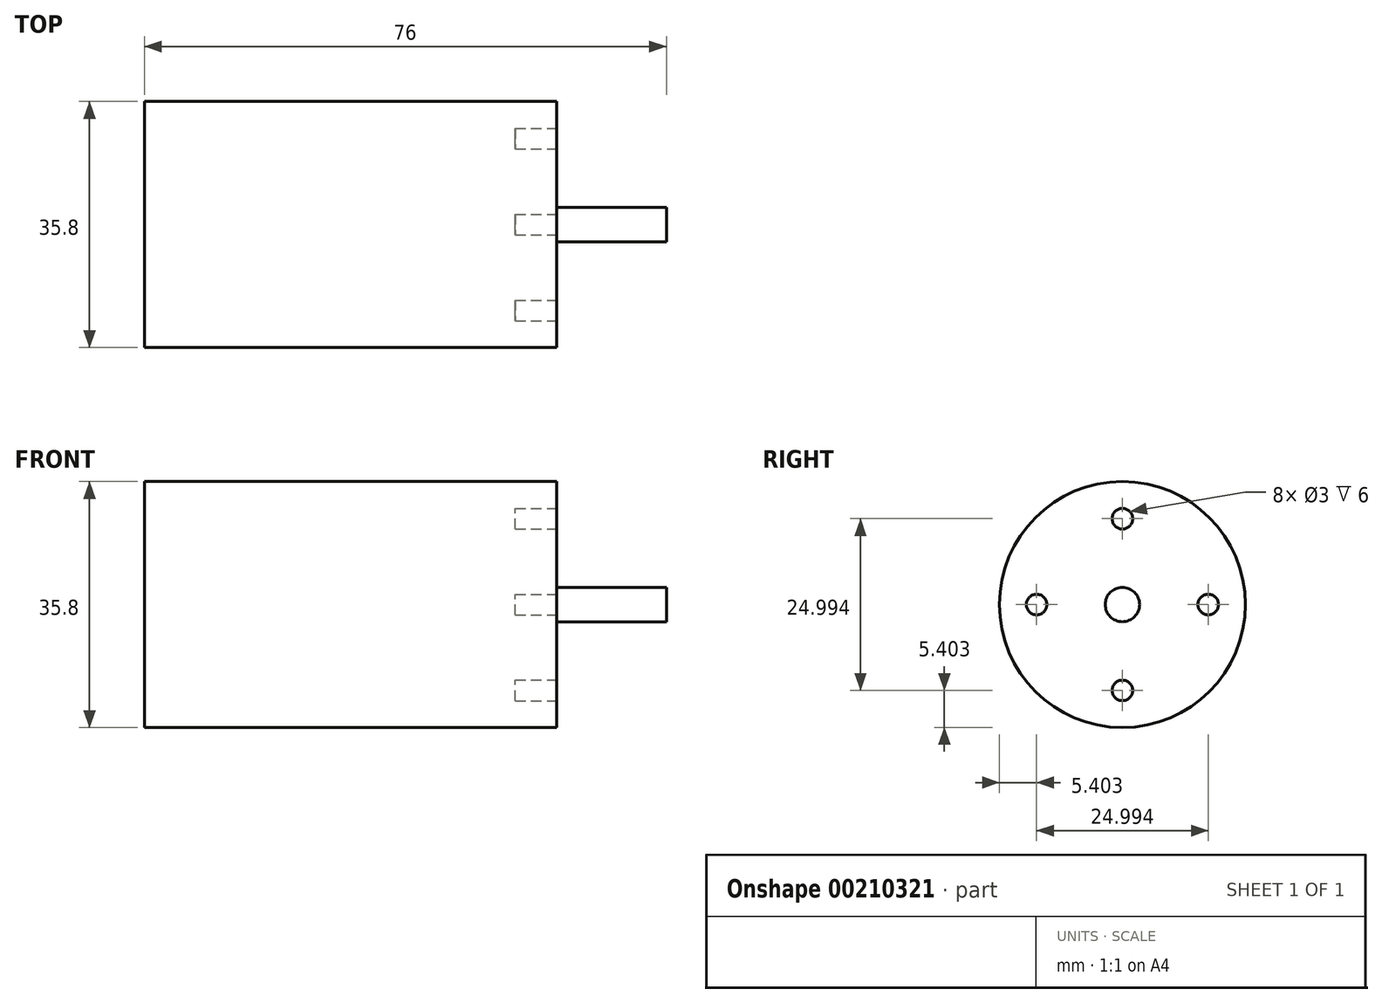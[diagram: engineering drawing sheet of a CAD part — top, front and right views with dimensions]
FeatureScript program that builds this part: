
annotation { "Feature Type Name" : "Feature", "Feature Type Description" : "" }
export const myFeature = defineFeature(function(context is Context, id is Id, definition is map)
    precondition{}
    {
        {
            var Q0;
            Q0=qCreatedBy(makeId("Right.planeOp"),FACE);
            var sketch = newSketch(context, id + "F0", { "sketchPlane" : qUnion([Q0])});
            skCircle(sketch, "E0", {"center": v(0, 0) * mm, "radius": 17.9 * mm});
            skSolve(sketch);
        }
        {
            var Q0;
            Q0 = qSketchRegion(id + "F0", true);
            extrude(context, id + "F1", {"entities" : qUnion([Q0]), "endBound" : BoundingType.SYMMETRIC, "depth" : 60 * mm});
        }
        {
            var Q0;
            Q0=makeQuery(id+"F1.opExtrude","CAP_FACE",FACE,{"disambiguationData":[OSD([sQuery(id+"F0.wireOp",EDGE,"E0")])],"isStart":false});
            var sketch = newSketch(context, id + "F2", { "sketchPlane" : qUnion([Q0])});
            skCircle(sketch, "E1", {"center": v(0, 0) * mm, "radius": 2.5 * mm});
            skSolve(sketch);
        }
        {
            var Q0;
            Q0 = qSketchRegion(id + "F2", true);
            extrude(context, id + "F3", {"entities" : qUnion([Q0]), "operationType" : NewBodyOperationType.ADD, "depth" : 16 * mm});
        }
        {
            var Q0;
            Q0=makeQuery(id+"F1.opExtrude","CAP_FACE",FACE,{"disambiguationData":[OSD([sQuery(id+"F0.wireOp",EDGE,"E0")])],"isStart":false});
            var sketch = newSketch(context, id + "F4", { "sketchPlane" : qUnion([Q0])});
            skCircle(sketch, "E2", {"center": v(0, 0) * mm, "radius": 12.5 * mm, "construction": true});
            skCircle(sketch, "E3", {"center": v(0, 12.5) * mm, "radius": 1.5 * mm});
            skCircle(sketch, "E4.1.0", {"center": v(-12.5, 0) * mm, "radius": 1.5 * mm});
            skCircle(sketch, "E4.2.0", {"center": v(0, -12.5) * mm, "radius": 1.5 * mm});
            skCircle(sketch, "E4.3.0", {"center": v(12.5, 0) * mm, "radius": 1.5 * mm});
            skSolve(sketch);
        }
        {
            var Q0;
            Q0 = qSketchRegion(id + "F4", true);
            extrude(context, id + "F5", {"entities" : qUnion([Q0]), "operationType" : NewBodyOperationType.REMOVE, "oppositeDirection" : true, "depth" : 6 * mm});
        }
        {
            var Q0;
            Q0=makeQuery(id+"F1.opExtrude","SWEPT_BODY",BODY,{"disambiguationData":[OSD([sQuery(id+"F0.wireOp",EDGE,"E0")])]});
            transform(context, id + "F6", {"entities" : qUnion([Q0]), "transformType" : TransformType.TRANSLATION_3D, "dx" : 0 * mm, "dy" : 0 * mm, "dz" : 0 * mm, "makeCopy" : true});
        }
    });
